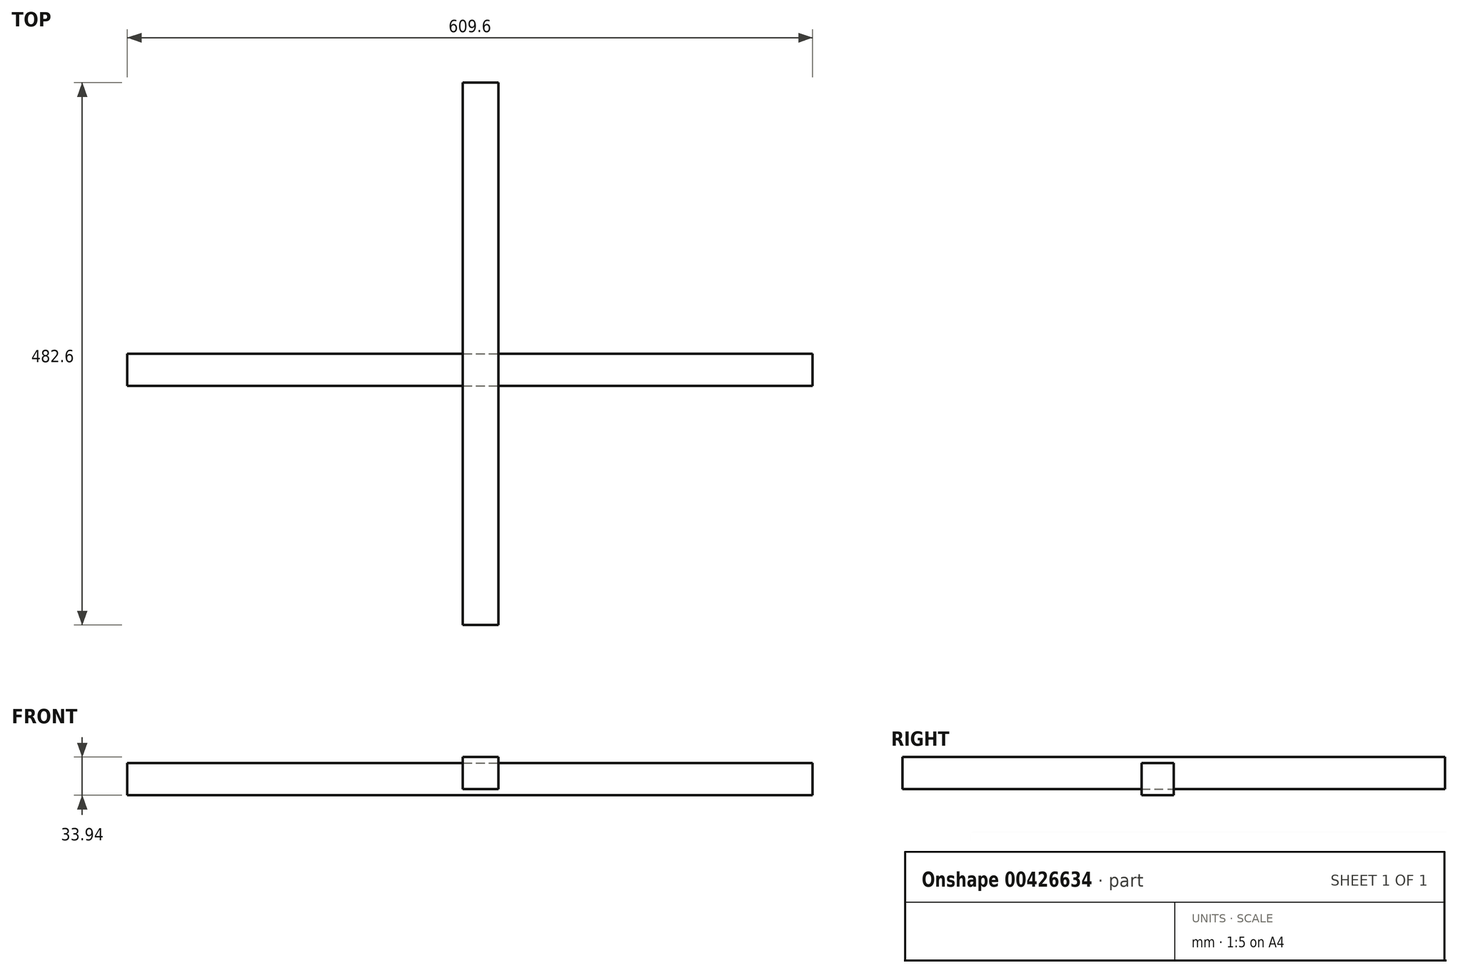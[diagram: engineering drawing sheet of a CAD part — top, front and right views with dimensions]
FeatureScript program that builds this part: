
annotation { "Feature Type Name" : "Feature", "Feature Type Description" : "" }
export const myFeature = defineFeature(function(context is Context, id is Id, definition is map)
    precondition{}
    {
        {
            var Q0;
            Q0=qCreatedBy(makeId("Front.planeOp"),FACE);
            var sketch = newSketch(context, id + "F0", { "sketchPlane" : qUnion([Q0])});
            skLineSegment(sketch, "E0.bottom", {"start": v(-298.46, 8.92) * mm, "end": v(311.14, 8.92) * mm});
            skLineSegment(sketch, "E0.top", {"start": v(-298.46, -19.65) * mm, "end": v(311.14, -19.65) * mm});
            skLineSegment(sketch, "E0.left", {"start": v(-298.46, 8.92) * mm, "end": v(-298.46, -19.65) * mm});
            skLineSegment(sketch, "E0.right", {"start": v(311.14, 8.92) * mm, "end": v(311.14, -19.65) * mm});
            skSolve(sketch);
        }
        {
            var Q0;
            Q0=makeQuery(id+"F0.imprint","IMPRINT",FACE,{"disambiguationData":[TD([[makeQuery(id+"F0.imprint","IMPRINT",EDGE,{"derivedFrom":sQuery(id+"F0.wireOp",EDGE,"E0.bottom")}),-1.0]])]});
            extrude(context, id + "F1", {"entities" : qUnion([Q0]), "depth" : 28.57 * mm, "offsetDistance" : 25.4 * mm});
        }
        {
            var Q0;
            Q0=qCreatedBy(makeId("Right.planeOp"),FACE);
            var sketch = newSketch(context, id + "F2", { "sketchPlane" : qUnion([Q0])});
            skLineSegment(sketch, "E1.bottom", {"start": v(-241.3, 14.29) * mm, "end": v(241.3, 14.29) * mm});
            skLineSegment(sketch, "E1.top", {"start": v(-241.3, -14.29) * mm, "end": v(241.3, -14.29) * mm});
            skLineSegment(sketch, "E1.left", {"start": v(-241.3, 14.29) * mm, "end": v(-241.3, -14.29) * mm});
            skLineSegment(sketch, "E1.right", {"start": v(241.3, 14.29) * mm, "end": v(241.3, -14.29) * mm});
            skPoint(sketch, "E1.middle", {"position": v(0, 0) * mm});
            skSolve(sketch);
        }
        {
            var Q0;
            Q0 = qSketchRegion(id + "F2", true);
            extrude(context, id + "F3", {"entities" : qUnion([Q0]), "depth" : 31.75 * mm, "offsetDistance" : 25.4 * mm});
        }
    });
